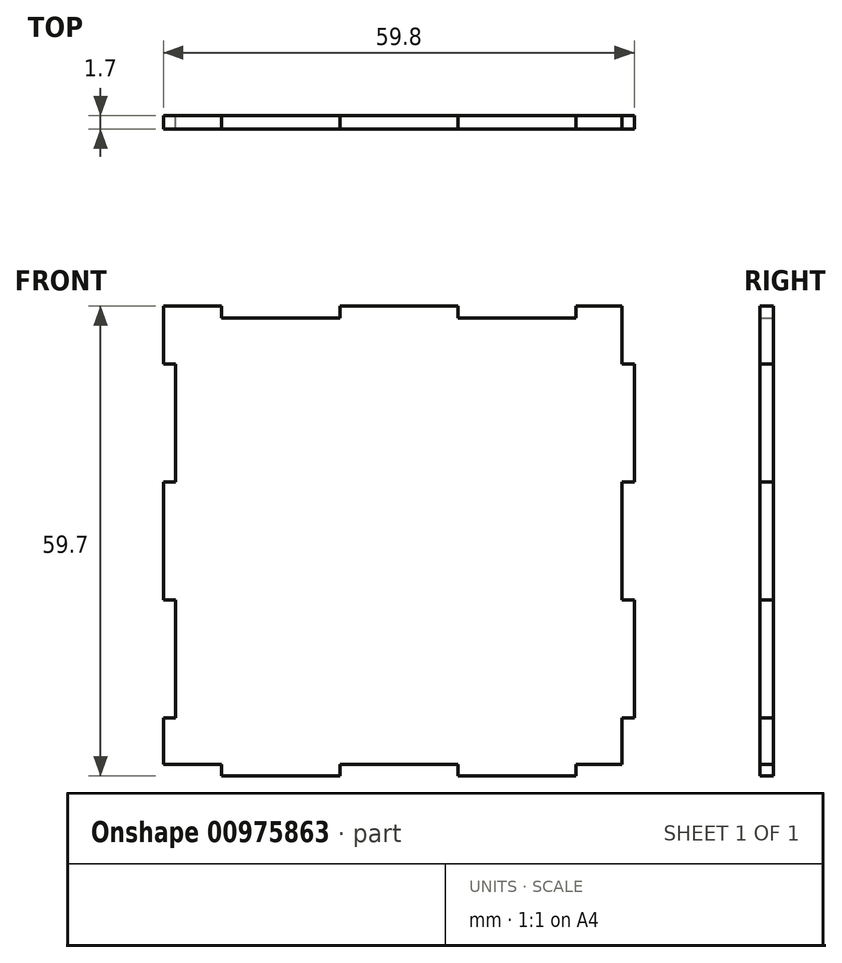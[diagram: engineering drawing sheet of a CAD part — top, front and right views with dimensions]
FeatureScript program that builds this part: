
annotation { "Feature Type Name" : "Feature", "Feature Type Description" : "" }
export const myFeature = defineFeature(function(context is Context, id is Id, definition is map)
    precondition{}
    {
        {
            var Q0;
            Q0=qCreatedBy(makeId("Front.planeOp"),FACE);
            var sketch = newSketch(context, id + "F0", { "sketchPlane" : qUnion([Q0])});
            skLineSegment(sketch, "E0.bottom", {"start": v(29.9, 29.85) * mm, "end": v(-29.9, 29.85) * mm, "construction": true});
            skLineSegment(sketch, "E0.top", {"start": v(29.9, -29.85) * mm, "end": v(-29.9, -29.85) * mm, "construction": true});
            skLineSegment(sketch, "E0.left", {"start": v(29.9, 29.85) * mm, "end": v(29.9, -29.85) * mm, "construction": true});
            skLineSegment(sketch, "E0.right", {"start": v(-29.9, 29.85) * mm, "end": v(-29.9, -29.85) * mm, "construction": true});
            skPoint(sketch, "E0.middle", {"position": v(0, 0) * mm});
            skLineSegment(sketch, "E1.bottom", {"start": v(28.35, 28.35) * mm, "end": v(-28.35, 28.35) * mm, "construction": true});
            skLineSegment(sketch, "E1.top", {"start": v(28.35, -28.35) * mm, "end": v(-28.35, -28.35) * mm, "construction": true});
            skLineSegment(sketch, "E1.left", {"start": v(28.35, 28.35) * mm, "end": v(28.35, -28.35) * mm, "construction": true});
            skLineSegment(sketch, "E1.right", {"start": v(-28.35, 28.35) * mm, "end": v(-28.35, -28.35) * mm, "construction": true});
            skLineSegment(sketch, "E2", {"start": v(0, 49.44) * mm, "end": v(0, -51.53) * mm, "construction": true});
            skLineSegment(sketch, "E3", {"start": v(-44.2, 0) * mm, "end": v(59.04, 0) * mm, "construction": true});
            skLineSegment(sketch, "E4", {"start": v(-29.9, 29.85) * mm, "end": v(-22.5, 29.85) * mm});
            skLineSegment(sketch, "E5", {"start": v(-22.5, 29.85) * mm, "end": v(-22.5, 28.35) * mm});
            skLineSegment(sketch, "E6", {"start": v(-22.5, 28.35) * mm, "end": v(-7.5, 28.35) * mm});
            skLineSegment(sketch, "E7", {"start": v(-7.5, 28.35) * mm, "end": v(-7.5, 29.85) * mm});
            skLineSegment(sketch, "E8", {"start": v(-7.5, 29.85) * mm, "end": v(7.5, 29.85) * mm});
            skLineSegment(sketch, "E9", {"start": v(7.5, 29.85) * mm, "end": v(7.5, 28.35) * mm});
            skLineSegment(sketch, "E10", {"start": v(7.5, 28.35) * mm, "end": v(22.5, 28.35) * mm});
            skLineSegment(sketch, "E11", {"start": v(22.5, 28.35) * mm, "end": v(22.5, 29.85) * mm});
            skLineSegment(sketch, "E12", {"start": v(-7.5, -29.85) * mm, "end": v(-7.5, -28.35) * mm});
            skLineSegment(sketch, "E13", {"start": v(-7.5, -28.35) * mm, "end": v(7.5, -28.35) * mm});
            skLineSegment(sketch, "E14", {"start": v(7.5, -28.35) * mm, "end": v(7.5, -29.85) * mm});
            skLineSegment(sketch, "E15", {"start": v(7.5, -29.85) * mm, "end": v(22.5, -29.85) * mm});
            skLineSegment(sketch, "E16", {"start": v(22.5, -29.85) * mm, "end": v(22.5, -28.35) * mm});
            skLineSegment(sketch, "E17", {"start": v(-7.5, -29.85) * mm, "end": v(-22.5, -29.85) * mm});
            skLineSegment(sketch, "E18", {"start": v(-22.5, -29.85) * mm, "end": v(-22.5, -28.35) * mm});
            skLineSegment(sketch, "E19", {"start": v(-29.9, -7.5) * mm, "end": v(-29.9, 7.5) * mm});
            skLineSegment(sketch, "E20", {"start": v(-29.9, 7.5) * mm, "end": v(-28.35, 7.5) * mm});
            skLineSegment(sketch, "E21", {"start": v(-28.35, 7.5) * mm, "end": v(-28.35, 22.5) * mm});
            skLineSegment(sketch, "E22", {"start": v(-28.35, 22.5) * mm, "end": v(-29.9, 22.5) * mm});
            skLineSegment(sketch, "E23", {"start": v(-29.9, 22.5) * mm, "end": v(-29.9, 29.85) * mm});
            skLineSegment(sketch, "E24", {"start": v(-29.9, -7.5) * mm, "end": v(-28.35, -7.5) * mm});
            skLineSegment(sketch, "E25", {"start": v(-28.35, -7.5) * mm, "end": v(-28.35, -22.5) * mm});
            skLineSegment(sketch, "E26", {"start": v(-28.35, -22.5) * mm, "end": v(-29.9, -22.5) * mm});
            skLineSegment(sketch, "E27", {"start": v(-29.9, -22.5) * mm, "end": v(-29.9, -28.35) * mm});
            skLineSegment(sketch, "E28", {"start": v(-22.5, -28.35) * mm, "end": v(-29.9, -28.35) * mm});
            skLineSegment(sketch, "E29", {"start": v(22.5, 29.85) * mm, "end": v(28.35, 29.85) * mm});
            skLineSegment(sketch, "E30", {"start": v(28.35, 29.85) * mm, "end": v(28.35, 22.5) * mm});
            skLineSegment(sketch, "E31", {"start": v(28.35, 22.5) * mm, "end": v(29.9, 22.5) * mm});
            skLineSegment(sketch, "E32", {"start": v(29.9, 22.5) * mm, "end": v(29.9, 7.5) * mm});
            skLineSegment(sketch, "E33", {"start": v(29.9, 7.5) * mm, "end": v(28.35, 7.5) * mm});
            skLineSegment(sketch, "E34", {"start": v(28.35, 7.5) * mm, "end": v(28.35, -7.5) * mm});
            skLineSegment(sketch, "E35", {"start": v(28.35, -7.5) * mm, "end": v(29.9, -7.5) * mm});
            skLineSegment(sketch, "E36", {"start": v(29.9, -7.5) * mm, "end": v(29.9, -22.5) * mm});
            skLineSegment(sketch, "E37", {"start": v(29.9, -22.5) * mm, "end": v(28.35, -22.5) * mm});
            skLineSegment(sketch, "E38", {"start": v(22.5, -28.35) * mm, "end": v(28.35, -28.35) * mm});
            skLineSegment(sketch, "E39", {"start": v(28.35, -22.5) * mm, "end": v(28.35, -28.35) * mm});
            skSolve(sketch);
        }
        {
            var Q0;
            Q0=makeQuery(id+"F0.imprint","IMPRINT",FACE,{"disambiguationData":[TD([[makeQuery(id+"F0.imprint","IMPRINT",EDGE,{"derivedFrom":sQuery(id+"F0.wireOp",EDGE,"E4")}),-1.0]])]});
            extrude(context, id + "F1", {"entities" : qUnion([Q0]), "depth" : 1.7 * mm, "offsetDistance" : 25 * mm});
        }
    });
